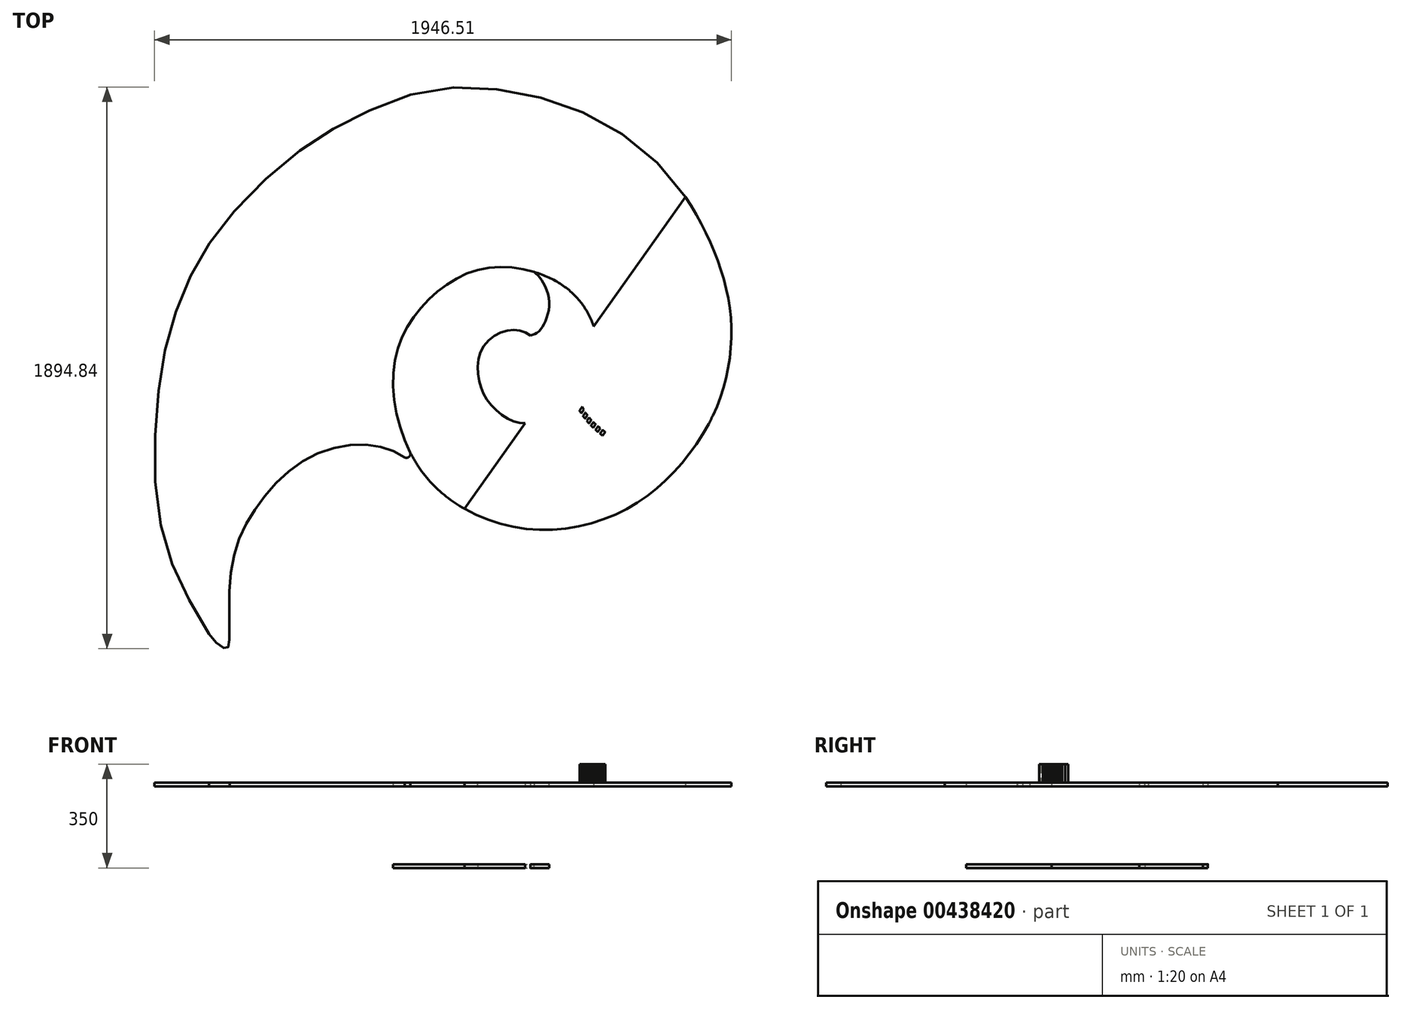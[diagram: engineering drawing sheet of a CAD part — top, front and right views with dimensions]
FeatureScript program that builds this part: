
annotation { "Feature Type Name" : "Feature", "Feature Type Description" : "" }
export const myFeature = defineFeature(function(context is Context, id is Id, definition is map)
    precondition{}
    {
        {
            var Q0;
            Q0=qCreatedBy(makeId("Top.planeOp"),FACE);
            var sketch = newSketch(context, id + "F0", { "sketchPlane" : qUnion([Q0])});
            skFitSpline(sketch, "E0", {"points": [v(-973.16, -759.52) * mm, v(-1084.07, -553.93) * mm, v(-1149, -313.17) * mm, v(-1149, 0) * mm, v(-1108.42, 252.2) * mm, v(-1027.26, 463.21) * mm, v(-902.82, 649.87) * mm, v(-689.12, 855.46) * mm, v(-483.52, 982.6) * mm, v(-221.12, 1077.28) * mm, v(60.21, 1069.17) * mm, v(338.85, 977.2) * mm, v(576.9, 790.54) * mm, v(722.98, 552.48) * mm, v(787.9, 309.02) * mm, v(755.44, 46.62) * mm, v(631, -172.5) * mm, v(436.23, -337.52) * mm, v(152.19, -407.85) * mm, v(-131.85, -323.99) * mm, v(-304.98, -123.8) * mm, v(-345.56, 165.64) * mm, v(-240.06, 360.42) * mm, v(-58.81, 471.33) * mm, v(146.78, 455.1) * mm, v(282.04, 359.86) * mm, v(338.85, 221.9) * mm, v(325.32, 97.45) * mm, v(265.8, 14.95) * mm, v(190.06, -39.16) * mm, v(117.02, -48.62) * mm, v(49.4, -39.16) * mm, v(-26.35, 20.36) * mm, v(-62.87, 101.51) * mm, v(-52.05, 201.6) * mm, v(25.05, 262.47) * mm, v(98.09, 257.06) * mm, v(138.66, 213.78) * mm, v(137.3, 168.3) * mm, v(107.15, 145.37) * mm, v(78.2, 151.4) * mm, v(76.99, 171.91) * mm, v(93.48, 175.53) * mm, v(105.94, 164.27) * mm], "startDerivative": vector(-4291.53, 7207.06) * mm, "endDerivative": vector(1408.44, -1875.62) * mm});
            skLineSegment(sketch, "E1", {"start": v(-745.3, -1232.6) * mm, "end": v(1330.3, 1696.97) * mm});
            skFitSpline(sketch, "E2", {"points": [v(-265.46, -195.32) * mm, v(-394.45, -127.48) * mm, v(-611.6, -151.61) * mm, v(-801.4, -315.68) * mm, v(-897.91, -540.87) * mm, v(-904.35, -782.14) * mm, v(-916.2, -808.47) * mm, v(-973.16, -759.52) * mm], "startDerivative": vector(-874.47, 621.9) * mm, "endDerivative": vector(-467.5, 747.47) * mm});
            skArc(sketch, "E3", {"start": v(-313.13, -162.85) * mm, "mid": v(-297.56, -161.17) * mm, "end": v(-294.52, -145.82) * mm});
            skFitSpline(sketch, "E4", {"points": [v(138.66, 213.78) * mm, v(165.04, 213.78) * mm, v(201.68, 229.46) * mm, v(240.18, 276.77) * mm, v(255.95, 328.71) * mm, v(251, 393.28) * mm], "startDerivative": vector(171.88, -13.91) * mm, "endDerivative": vector(-42.45, 286.73) * mm});
            skFitSpline(sketch, "E5", {"points": [v(111.73, 248.6) * mm, v(136.42, 259.02) * mm, v(160.7, 293.13) * mm, v(175.12, 364.62) * mm, v(149.54, 434.8) * mm, v(124.07, 462.73) * mm], "startDerivative": vector(173.6, 49.14) * mm, "endDerivative": vector(-145.97, 131.68) * mm});
            skFitSpline(sketch, "E6", {"points": [v(142.66, 194.93) * mm, v(148.69, 175.58) * mm, v(167.7, 162.14) * mm, v(215.26, 158.86) * mm, v(238.22, 162.8) * mm, v(257.57, 173.29) * mm, v(299.55, 220.52) * mm, v(322.28, 287.46) * mm], "startDerivative": vector(37.43, -192.33) * mm, "endDerivative": vector(77.95, 345.79) * mm});
            skFitSpline(sketch, "E7", {"points": [v(265.8, 14.95) * mm, v(306.23, -44.99) * mm, v(407.72, -117.8) * mm, v(559.96, -124.41) * mm, v(713.53, -49.85) * mm], "startDerivative": vector(177.95, -311.5) * mm, "endDerivative": vector(514.38, 315.67) * mm});
            skFitSpline(sketch, "E8", {"points": [v(281.02, 30.69) * mm, v(286.53, 8.54) * mm, v(306.2, -23.93) * mm, v(339, -57.71) * mm, v(388.52, -92.48) * mm, v(449.53, -113.14) * mm, v(521.3, -114.3) * mm, v(585.91, -96.92) * mm, v(727.34, -22.5) * mm], "startDerivative": vector(47.5, -281.27) * mm, "endDerivative": vector(773.32, 437.32) * mm});
            skLineSegment(sketch, "E9", {"start": v(286.66, 8.2) * mm, "end": v(158.97, -172.04) * mm});
            skLineSegment(sketch, "E10.1.0.0", {"start": v(299.16, 8.2) * mm, "end": v(171.47, -172.04) * mm});
            skLineSegment(sketch, "E10.2.0.0", {"start": v(311.66, 8.2) * mm, "end": v(183.97, -172.04) * mm});
            skLineSegment(sketch, "E10.3.0.0", {"start": v(324.16, 8.2) * mm, "end": v(196.47, -172.04) * mm});
            skLineSegment(sketch, "E10.4.0.0", {"start": v(336.66, 8.2) * mm, "end": v(208.97, -172.04) * mm});
            skLineSegment(sketch, "E10.5.0.0", {"start": v(349.16, 8.2) * mm, "end": v(221.47, -172.04) * mm});
            skLineSegment(sketch, "E10.6.0.0", {"start": v(361.66, 8.2) * mm, "end": v(233.97, -172.04) * mm});
            skLineSegment(sketch, "E10.7.0.0", {"start": v(374.16, 8.2) * mm, "end": v(246.47, -172.04) * mm});
            skLineSegment(sketch, "E10.8.0.0", {"start": v(386.66, 8.2) * mm, "end": v(258.97, -172.04) * mm});
            skLineSegment(sketch, "E10.9.0.0", {"start": v(399.16, 8.2) * mm, "end": v(271.47, -172.04) * mm});
            skLineSegment(sketch, "E10.10.0.0", {"start": v(411.66, 8.2) * mm, "end": v(283.97, -172.04) * mm});
            skLineSegment(sketch, "E10.11.0.0", {"start": v(424.16, 8.2) * mm, "end": v(296.47, -172.04) * mm});
            skLineSegment(sketch, "E10.direction1", {"start": v(158.97, -172.04) * mm, "end": v(171.47, -172.04) * mm, "construction": true});
            skSolve(sketch);
        }
        {
            var Q0;
            {var subQ4=sQuery(id+"F0.wireOp",EDGE,"E3");Q0=makeQuery(id+"F0.imprint","IMPRINT",FACE,{"disambiguationData":[TD([[makeQuery(id+"F0.imprint","IMPRINT",EDGE,{"derivedFrom":subQ4}),1.0]])]});}
            extrude(context, id + "F1", {"entities" : qUnion([Q0]), "depth" : 12.5 * mm});
        }
        {
            var Q0;
            {var subQ1=sQuery(id+"F0.wireOp",EDGE,"E0");var subQ6=makeQuery(id+"F0.imprint","INTERSECT",VERTEX,{"disambiguationData":[OD(1.0)],"derivedFrom":[subQ1,sQuery(id+"F0.wireOp",EDGE,"E2")]});Q0=makeQuery(id+"F0.imprint","IMPRINT",FACE,{"disambiguationData":[TD([[makeQuery(id+"F0.imprint","IMPRINT",EDGE,{"disambiguationData":[TD([[subQ6,1.0]])],"derivedFrom":subQ1}),-1.0]])]});}
            extrude(context, id + "F2", {"entities" : qUnion([Q0]), "oppositeDirection" : true, "depth" : 275 * mm, "hasSecondDirection" : true, "secondDirectionOppositeDirection" : true, "secondDirectionDepth" : 262.5 * mm});
        }
        {
            var Q0;
            {var subQ0=sQuery(id+"F0.wireOp",EDGE,"E1");var subQ1=sQuery(id+"F0.wireOp",EDGE,"E0");var subQ2=makeQuery(id+"F0.imprint","INTERSECT",VERTEX,{"disambiguationData":[OD(0.0)],"derivedFrom":[subQ1,subQ0]});Q0=makeQuery(id+"F0.imprint","IMPRINT",FACE,{"disambiguationData":[TD([[makeQuery(id+"F0.imprint","IMPRINT",EDGE,{"disambiguationData":[TD([[subQ2,-1.0]])],"derivedFrom":subQ1}),-1.0]])]});}
            var Q1;
            {var subQ0=sQuery(id+"F0.wireOp",EDGE,"E1");var subQ1=sQuery(id+"F0.wireOp",EDGE,"E0");var subQ2=makeQuery(id+"F0.imprint","INTERSECT",VERTEX,{"disambiguationData":[OD(2.0)],"derivedFrom":[subQ1,subQ0]});Q1=makeQuery(id+"F0.imprint","IMPRINT",FACE,{"disambiguationData":[TD([[makeQuery(id+"F0.imprint","IMPRINT",EDGE,{"disambiguationData":[TD([[subQ2,1.0]])],"derivedFrom":subQ1}),-1.0]])]});}
            extrude(context, id + "F3", {"entities" : qUnion([Q0, Q1]), "depth" : 12.5 * mm});
        }
        {
            var Q0;
            {var subQ0=sQuery(id+"F0.wireOp",EDGE,"E8");Q0=makeQuery(id+"F0.imprint","IMPRINT",FACE,{"disambiguationData":[TD([[makeQuery(id+"F0.imprint","IMPRINT",EDGE,{"derivedFrom":subQ0}),1.0]])]});}
            var Q1;
            {var subQ0=sQuery(id+"F0.wireOp",EDGE,"E7");Q1=makeQuery(id+"F0.imprint","IMPRINT",FACE,{"disambiguationData":[TD([[makeQuery(id+"F0.imprint","IMPRINT",EDGE,{"derivedFrom":subQ0}),-1.0]])]});}
            var Q2;
            {var subQ1=sQuery(id+"F0.wireOp",EDGE,"E0");var subQ6=makeQuery(id+"F0.imprint","INTERSECT",VERTEX,{"disambiguationData":[OD(0.0)],"derivedFrom":[subQ1,sQuery(id+"F0.wireOp",EDGE,"E8")]});Q2=makeQuery(id+"F0.imprint","IMPRINT",FACE,{"disambiguationData":[TD([[makeQuery(id+"F0.imprint","IMPRINT",EDGE,{"disambiguationData":[TD([[subQ6,1.0]])],"derivedFrom":subQ1}),-1.0]])]});}
            var Q3;
            {var subQ0=sQuery(id+"F0.wireOp",EDGE,"E7");Q3=makeQuery(id+"F0.imprint","IMPRINT",FACE,{"disambiguationData":[TD([[makeQuery(id+"F0.imprint","IMPRINT",EDGE,{"derivedFrom":subQ0}),1.0]])]});}
            extrude(context, id + "F4", {"entities" : qUnion([Q0, Q1, Q2, Q3]), "depth" : 12.5 * mm});
        }
        {
            var Q0;
            {var subQ0=sQuery(id+"F0.wireOp",EDGE,"E9");var subQ1=sQuery(id+"F0.wireOp",EDGE,"E7");var subQ2=makeQuery(id+"F0.imprint","INTERSECT",VERTEX,{"derivedFrom":[subQ1,subQ0]});Q0=makeQuery(id+"F0.imprint","IMPRINT",FACE,{"disambiguationData":[TD([[makeQuery(id+"F0.imprint","IMPRINT",EDGE,{"disambiguationData":[TD([[subQ2,-1.0]])],"derivedFrom":subQ1}),1.0]])]});}
            var Q1;
            {var subQ0=sQuery(id+"F0.wireOp",EDGE,"E10.2.0.0");var subQ1=sQuery(id+"F0.wireOp",EDGE,"E7");var subQ2=makeQuery(id+"F0.imprint","INTERSECT",VERTEX,{"derivedFrom":[subQ1,subQ0]});Q1=makeQuery(id+"F0.imprint","IMPRINT",FACE,{"disambiguationData":[TD([[makeQuery(id+"F0.imprint","IMPRINT",EDGE,{"disambiguationData":[TD([[subQ2,-1.0]])],"derivedFrom":subQ1}),1.0]])]});}
            var Q2;
            {var subQ0=sQuery(id+"F0.wireOp",EDGE,"E10.4.0.0");var subQ1=sQuery(id+"F0.wireOp",EDGE,"E7");var subQ2=makeQuery(id+"F0.imprint","INTERSECT",VERTEX,{"derivedFrom":[subQ1,subQ0]});Q2=makeQuery(id+"F0.imprint","IMPRINT",FACE,{"disambiguationData":[TD([[makeQuery(id+"F0.imprint","IMPRINT",EDGE,{"disambiguationData":[TD([[subQ2,-1.0]])],"derivedFrom":subQ1}),1.0]])]});}
            var Q3;
            {var subQ0=sQuery(id+"F0.wireOp",EDGE,"E10.6.0.0");var subQ1=sQuery(id+"F0.wireOp",EDGE,"E7");var subQ2=makeQuery(id+"F0.imprint","INTERSECT",VERTEX,{"derivedFrom":[subQ1,subQ0]});Q3=makeQuery(id+"F0.imprint","IMPRINT",FACE,{"disambiguationData":[TD([[makeQuery(id+"F0.imprint","IMPRINT",EDGE,{"disambiguationData":[TD([[subQ2,-1.0]])],"derivedFrom":subQ1}),1.0]])]});}
            var Q4;
            {var subQ0=sQuery(id+"F0.wireOp",EDGE,"E10.8.0.0");var subQ1=sQuery(id+"F0.wireOp",EDGE,"E7");var subQ2=makeQuery(id+"F0.imprint","INTERSECT",VERTEX,{"derivedFrom":[subQ1,subQ0]});Q4=makeQuery(id+"F0.imprint","IMPRINT",FACE,{"disambiguationData":[TD([[makeQuery(id+"F0.imprint","IMPRINT",EDGE,{"disambiguationData":[TD([[subQ2,-1.0]])],"derivedFrom":subQ1}),1.0]])]});}
            var Q5;
            {var subQ0=sQuery(id+"F0.wireOp",EDGE,"E10.10.0.0");var subQ1=sQuery(id+"F0.wireOp",EDGE,"E7");var subQ2=makeQuery(id+"F0.imprint","INTERSECT",VERTEX,{"derivedFrom":[subQ1,subQ0]});Q5=makeQuery(id+"F0.imprint","IMPRINT",FACE,{"disambiguationData":[TD([[makeQuery(id+"F0.imprint","IMPRINT",EDGE,{"disambiguationData":[TD([[subQ2,-1.0]])],"derivedFrom":subQ1}),1.0]])]});}
            extrude(context, id + "F5", {"entities" : qUnion([Q0, Q1, Q2, Q3, Q4, Q5]), "operationType" : NewBodyOperationType.ADD, "depth" : 75 * mm});
        }
        {
            var Q0;
            {var subQ1=sQuery(id+"F0.wireOp",EDGE,"E0");var subQ7=makeQuery(id+"F0.imprint","INTERSECT",VERTEX,{"disambiguationData":[OD(0.0)],"derivedFrom":[subQ1,sQuery(id+"F0.wireOp",EDGE,"E5")]});Q0=makeQuery(id+"F0.imprint","IMPRINT",FACE,{"disambiguationData":[TD([[makeQuery(id+"F0.imprint","IMPRINT",EDGE,{"disambiguationData":[TD([[subQ7,1.0]])],"derivedFrom":subQ1}),-1.0]])]});}
            extrude(context, id + "F6", {"entities" : qUnion([Q0]), "depth" : 12.5 * mm});
        }
        {
            var Q0;
            {var subQ0=sQuery(id+"F0.wireOp",EDGE,"E5");Q0=makeQuery(id+"F0.imprint","IMPRINT",FACE,{"disambiguationData":[TD([[makeQuery(id+"F0.imprint","IMPRINT",EDGE,{"derivedFrom":subQ0}),1.0]])]});}
            extrude(context, id + "F7", {"entities" : qUnion([Q0]), "depth" : 12.5 * mm});
        }
        {
            var Q0;
            {var subQ4=sQuery(id+"F0.wireOp",EDGE,"E3");Q0=makeQuery(id+"F0.imprint","IMPRINT",FACE,{"disambiguationData":[TD([[makeQuery(id+"F0.imprint","IMPRINT",EDGE,{"derivedFrom":subQ4}),1.0]])]});}
            var Q1;
            {var subQ0=sQuery(id+"F0.wireOp",EDGE,"E4");Q1=makeQuery(id+"F0.imprint","IMPRINT",FACE,{"disambiguationData":[TD([[makeQuery(id+"F0.imprint","IMPRINT",EDGE,{"derivedFrom":subQ0}),-1.0]])]});}
            var Q2;
            {var subQ0=sQuery(id+"F0.wireOp",EDGE,"E4");Q2=makeQuery(id+"F0.imprint","IMPRINT",FACE,{"disambiguationData":[TD([[makeQuery(id+"F0.imprint","IMPRINT",EDGE,{"derivedFrom":subQ0}),1.0]])]});}
            var Q3;
            {var subQ0=sQuery(id+"F0.wireOp",EDGE,"E6");var subQ1=sQuery(id+"F0.wireOp",EDGE,"E0");var subQ2=makeQuery(id+"F0.imprint","INTERSECT",VERTEX,{"disambiguationData":[OD(1.0)],"derivedFrom":[subQ1,subQ0]});Q3=makeQuery(id+"F0.imprint","IMPRINT",FACE,{"disambiguationData":[TD([[makeQuery(id+"F0.imprint","IMPRINT",EDGE,{"disambiguationData":[TD([[subQ2,-1.0]])],"derivedFrom":subQ1}),-1.0]])]});}
            extrude(context, id + "F8", {"entities" : qUnion([Q0, Q1, Q2, Q3]), "depth" : 12.5 * mm});
        }
        {
            var Q0;
            {var subQ0=sQuery(id+"F0.wireOp",EDGE,"E6");var subQ1=sQuery(id+"F0.wireOp",EDGE,"E1");var subQ2=makeQuery(id+"F0.imprint","INTERSECT",VERTEX,{"disambiguationData":[OD(0.0)],"derivedFrom":[subQ1,subQ0]});Q0=makeQuery(id+"F0.imprint","IMPRINT",FACE,{"disambiguationData":[TD([[makeQuery(id+"F0.imprint","IMPRINT",EDGE,{"disambiguationData":[TD([[subQ2,-1.0]])],"derivedFrom":subQ1}),-1.0]])]});}
            extrude(context, id + "F9", {"entities" : qUnion([Q0]), "operationType" : NewBodyOperationType.ADD, "depth" : 12.5 * mm});
        }
    });
